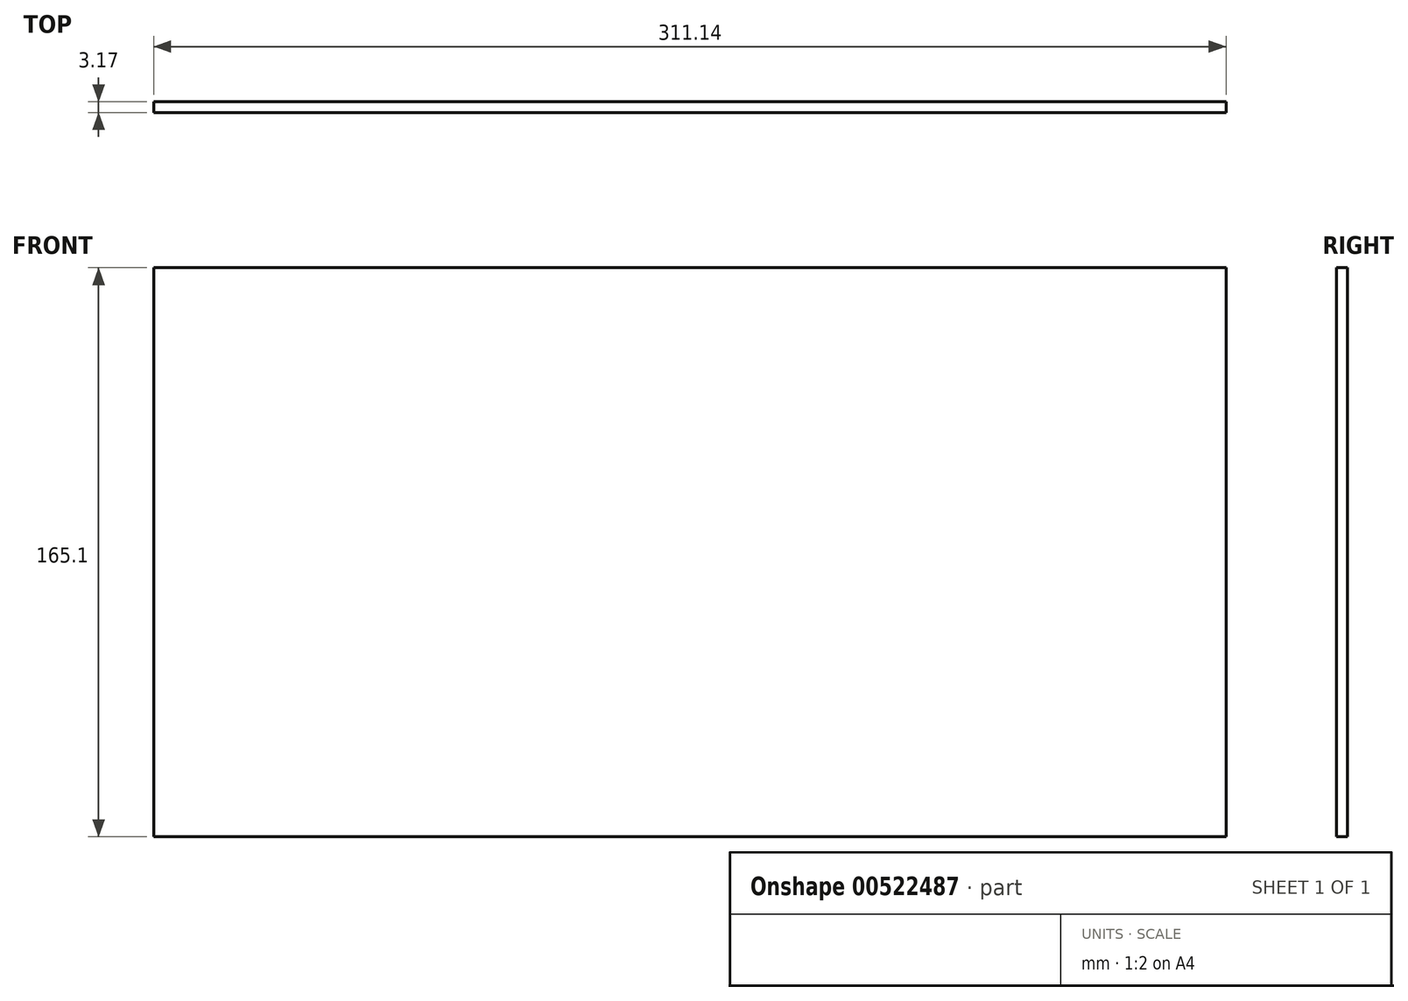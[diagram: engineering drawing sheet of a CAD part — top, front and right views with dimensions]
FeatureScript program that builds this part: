
annotation { "Feature Type Name" : "Feature", "Feature Type Description" : "" }
export const myFeature = defineFeature(function(context is Context, id is Id, definition is map)
    precondition{}
    {
        {
            var Q0;
            Q0=qCreatedBy(makeId("Front.planeOp"),FACE);
            var sketch = newSketch(context, id + "F0", { "sketchPlane" : qUnion([Q0])});
            skLineSegment(sketch, "E0.bottom", {"start": v(-155.58, 82.55) * mm, "end": v(155.58, 82.55) * mm});
            skLineSegment(sketch, "E0.top", {"start": v(-155.58, -82.55) * mm, "end": v(155.58, -82.55) * mm});
            skLineSegment(sketch, "E0.left", {"start": v(-155.57, 82.55) * mm, "end": v(-155.58, -82.55) * mm});
            skLineSegment(sketch, "E0.right", {"start": v(155.58, 82.55) * mm, "end": v(155.58, -82.55) * mm});
            skPoint(sketch, "E0.middle", {"position": v(0, 0) * mm});
            skSolve(sketch);
        }
        {
            var Q0;
            Q0=makeQuery(id+"F0.imprint","IMPRINT",FACE,{"disambiguationData":[TD([[makeQuery(id+"F0.imprint","IMPRINT",EDGE,{"derivedFrom":sQuery(id+"F0.wireOp",EDGE,"E0.bottom")}),-1.0]])]});
            extrude(context, id + "F1", {"entities" : qUnion([Q0]), "depth" : 3.17 * mm, "offsetDistance" : 25.4 * mm});
        }
    });
